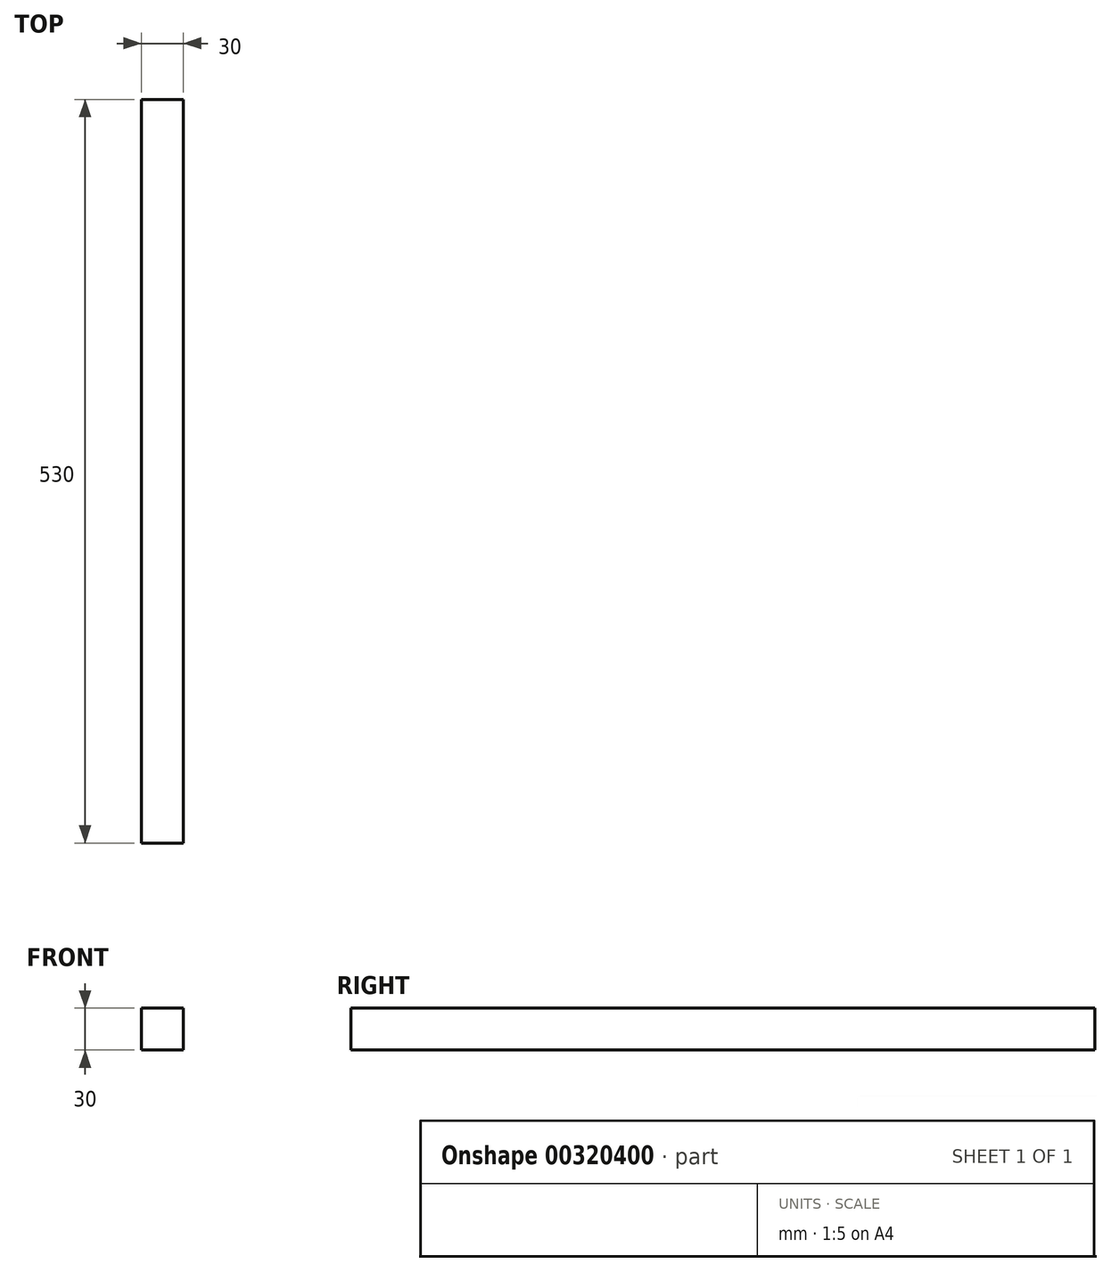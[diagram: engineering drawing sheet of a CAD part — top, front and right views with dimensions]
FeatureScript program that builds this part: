
annotation { "Feature Type Name" : "Feature", "Feature Type Description" : "" }
export const myFeature = defineFeature(function(context is Context, id is Id, definition is map)
    precondition{}
    {
        {
            var Q0;
            Q0=qCreatedBy(makeId("Front.planeOp"),FACE);
            var sketch = newSketch(context, id + "F0", { "sketchPlane" : qUnion([Q0])});
            skLineSegment(sketch, "E0.bottom", {"start": v(0, 0) * mm, "end": v(30, 0) * mm});
            skLineSegment(sketch, "E0.top", {"start": v(0, -30) * mm, "end": v(30, -30) * mm});
            skLineSegment(sketch, "E0.left", {"start": v(0, 0) * mm, "end": v(0, -30) * mm});
            skLineSegment(sketch, "E0.right", {"start": v(30, 0) * mm, "end": v(30, -30) * mm});
            skSolve(sketch);
        }
        {
            var Q0;
            Q0 = qSketchRegion(id + "F0", true);
            extrude(context, id + "F1", {"entities" : qUnion([Q0]), "depth" : 530 * mm});
        }
    });
